# Revit family: DCS_BC25_Beverage_Chiller_90000793A
name_source: partatom
category: Specialty Equipment
revit_build: Autodesk Revit 2018 (Build: 20170223_1515(x64)
units: mm (PartAtom-declared; Revit-internal decimal feet)

## family parameters
Always vertical = Yes
Cut with Voids When Loaded = Yes
OmniClass Number = 23.40.40.14.24.11
OmniClass Title = Bar Equipment
Part Type = Normal
Room Calculation Point = No
Round Connector Dimension = Use Diameter
Shared = No
Work Plane-Based = No

## types (2) — shared parameters
Cavity - Depth = 535 mm  [stored 1.75525 ft]
Cavity - Height = 250 mm  [stored 0.82021 ft]
Cavity - Width = 615 mm  [stored 2.01772 ft]
Manufacturer = Fisher & Paykel
Material - Body = DCS - Stainless Steel
Product - Depth = 557 mm  [stored 1.82743 ft]
Product - Height = 306 mm  [stored 1.00394 ft]
Product - Width = 670 mm  [stored 2.19816 ft]
URL = www.dcsappliances.com
Visibility - Clearance Required = Yes

## per-type parameters (varying)
| type | Description | Model | Visibility - Cover |
| Bottle Chiller | BC25 Bottle Chiller | BC25 | Yes |
| Bottle Chiller (without cover) | BC25 Beverage Chiller Bottle Holder Accessory | BC1-25AC | No |

note: [stored X ft] marks values corroborated as IEEE doubles in the binary element streams (Revit-internal decimal feet)

## geometry (parser evidence)
native form markers: Sweep x8
no freeform markers — native parametric forms only
